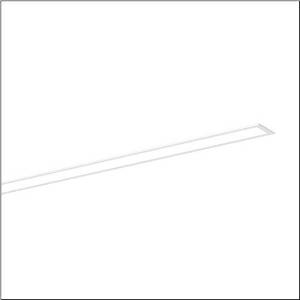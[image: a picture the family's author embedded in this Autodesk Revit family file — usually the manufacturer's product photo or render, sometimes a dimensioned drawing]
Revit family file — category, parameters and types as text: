
# Revit family: silica_r__21_51mx10dc45wb_eef5
name_source: partatom
category: Lighting Fixtures
units: mm (PartAtom-declared; Revit-internal decimal feet)

## family parameters
Cut with Voids When Loaded = No
Host = Face
Light Source = No
Part Type = Normal
Room Calculation Point = No
Round Connector Dimension = Use Diameter
Shared = No

## types (1)
- --- (1 x LED, 6000 lm, 40.1 W, 4000K)
    Apparent Load = 40 VA
    CIE Flux Codes = 48 79 96 100 100
    Color Rendering = 80
    Color Temperature = 4000K
    Default Elevation = 1800 mm
    Description = Silica® 21, office luminaire, primary optical cover: cover, of PMMA, opal, light emission: direct distribution, primary light characteristic: symmetric, installation type: recessed, LED, rated luminous flux: 6.000lm, luminous efficacy: 150lm/W, light colour: 840, colour temperature: 4000K, control gear: DALI 2, with terminal, 3+2-pole, max. 2.5mm², mains connection: 220..240V, AC, 50/60Hz, rated input power: 40.1W, luminaire housing, of aluminium, traffic white (RAL 9016), length: 3.028mm, width: 79mm, height: 53mm, protection rating (complete): IP20, insulation class (complete): insulation class I (protective earthing), certification: CE, ENEC, VDE, permissible operating ambient temperature: 0..+35°C, standard: EN 50419, packaging unit: 1 piece
    Height = 0 mm  [stored 0 ft]
    Lamp = 1 x LED
    Lamp Light Flux = 6000 lm
    Lamp Power = 40.1 W
    Lamp count = 1
    Length = 3027 mm
    Luminous efficacy = 150 lm/W
    Manufacturer = Siteco
    ModVariant = No
    Model = 51MX10DC45WB
    Mounting Place = Ceiling
    Mounting Type = Recessed
    Number of Poles = 1
    OnlyDefault = Yes
    Power Factor = 1
    Product Name = Silica® 21
    Product group = office luminaire | ceiling recessed
    ProductGroupID = 401
    Protection Class = Protection class I
    Protection Degree = IP 20
    RLX_Detail_Level = 1
    RLX_Emergency_Light_Flux = 0 lm
    RLX_Emergency_Type = 0
    RLX_Emergency_Type_DB = No
    RlxData = <blob elided: 21185 chars, md5=6e63d026>
    Socket = socket
    Standby Power = 0 W
    System Light Flux = 6000 lm
    System Power = 40 W
    Type Comments = factory setting: luminous flux: 100 % | dim-lin: 254 | 218 mA
    Type Image = l_1335891.jpg
    URL = http://relux.com
    VarID = @adj_117554
    Voltage = 0 V
    Weight = 0.00 kg
    Width = 79 mm

note: [stored X ft] marks values corroborated as IEEE doubles in the binary element streams (Revit-internal decimal feet)

## geometry (parser evidence)
native form markers: Blend x4, Sweep x10
no freeform markers — native parametric forms only
